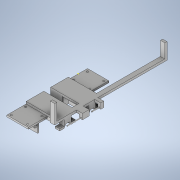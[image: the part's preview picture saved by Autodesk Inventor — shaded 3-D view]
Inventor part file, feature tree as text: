
AUTODESK INVENTOR PART (.ipt)
format: ipt  version: 2020.2 (Build 242310000, 310)  size: 751,104 bytes
history: native  units: mm
features: sketch x33, extrude x33, projected_geometry x12, hole x3
ambient origin geometry x8: Origin, YZ Plane, XZ Plane, XY Plane, X Axis, Y Axis, Z Axis, Center Point
bodies: Solid1 (feature_tree)
feature tree (81):
  sketch  "Sketch1"  dims[d0=8.0mm d1=98.298mm]
  extrude  "Extrusion1"  Depth=98.298mm
  extrude  "Extrusion2"  Depth=4.0mm
  extrude  "Extrusion3"  Depth=4.0mm TaperAngle=0.0deg
  extrude  "Extrusion4"  Depth=34.0mm
  extrude  "Extrusion5"  Depth=12.7mm
  extrude  "Extrusion6"  Depth=25.0mm
  hole  "Hole1"  [1 undecoded]
  extrude  "Extrusion11"  TaperAngle=60.0deg  [1 undecoded]
  extrude  "Extrusion12"  TaperAngle=120.0deg  [1 undecoded]
  sketch  "Sketch16"  dims[d19=6.4262mm d20=120.0deg]
  extrude  "Extrusion13"  Depth=6.4262mm
  extrude  "Extrusion14"  Depth=6.4262mm
  sketch  "Sketch17"  dims[d21=120.0deg d22=6.4262mm]
  extrude  "Extrusion15"  Depth=25.4mm TaperAngle=0.0deg
  extrude  "Extrusion18"  Depth=6.0mm
  extrude  "Extrusion19"  Depth=8.89mm
  extrude  "Extrusion20"  Depth=10.0mm
  hole  "Hole2"  [1 undecoded]
  extrude  "Extrusion21"  Depth=2.0mm
  extrude  "Extrusion22"  Depth=2.0mm
  sketch  "Sketch27"  dims[d45=8.89mm d46=2.0mm]
  extrude  "Extrusion23"  Depth=25.4mm
  extrude  "Extrusion24"  Depth=32.48mm
  extrude  "Extrusion25"  TaperAngle=90.0deg  [1 undecoded]
  sketch  "Sketch29"  dims[d79=51.53mm d80=32.48mm]
  extrude  "Extrusion26"  Depth=2.0mm
  extrude  "Extrusion27"  Depth=21.0mm
  extrude  "Extrusion28"  Depth=36.0mm TaperAngle=0.0deg
  extrude  "Extrusion29"  Depth=8.0mm
  extrude  "Extrusion30"  Depth=17.5mm
  extrude  "Extrusion32"  Depth=35.0mm
  extrude  "Extrusion33"  Depth=5.0mm
  extrude  "Extrusion34"  TaperAngle=90.0deg  [1 undecoded]
  extrude  "Extrusion35"  Depth=5.0mm
  extrude  "Extrusion38"  Depth=25.4mm TaperAngle=0.0deg
  extrude  "Extrusion39"  Depth=1.5mm
  extrude  "Extrusion40"  TaperAngle=0.0deg  [1 undecoded]
  hole  "Hole4"  [1 undecoded]
  extrude  "Extrusion43"  Depth=28.8036mm
  extrude  "Extrusion44"  Depth=25.4mm TaperAngle=0.0deg
  sketch  "Sketch2"  dims[d2=8.0mm d3=4.0mm]
  sketch  "Sketch3"  dims[d4=4.0mm d5=4.0mm d6=0.0mm]
  sketch  "Sketch4"  dims[d7=34.0mm d8=0.0mm d9=19.558mm]
  sketch  "Sketch5"  dims[d10=16.1125mm d11=12.7mm]
  sketch  "Sketch6"  dims[d12=25.0mm d13=0.0mm d14=11.1125mm]
  sketch  "Sketch14"  dims[d15=6.4135mm d16=12.827mm]
  projected_geometry  "Projected Loop2"
  sketch  "Sketch15"  dims[d17=6.4262mm d18=60.0deg]
  projected_geometry  "Projected Loop3"
  sketch  "Sketch18"  dims[d23=120.0deg d24=6.4262mm]
  sketch  "Sketch21"  dims[d25=120.0deg d26=25.4mm d27=0.0mm]
  sketch  "Sketch22"  dims[d28=6.0mm d29=8.89mm]
  sketch  "Sketch23"  dims[d30=5.9944mm d31=8.89mm]
  sketch  "Sketch24"  dims[d32=25.4mm d33=0.0mm d34=10.0mm]
  sketch  "Sketch25"  dims[d35=90.0deg d36=20.0mm]
  projected_geometry  "Projected Loop5"
  sketch  "Sketch26"  dims[d37=3.4mm d38=19.05mm d39=6.2992mm d40=6.35mm d41=90.0deg d42=5.0mm d43=0.0mm d44=2.0mm]
  sketch  "Sketch28"  dims[d47=25.4mm d48=0.0mm d78=16.24mm]
  sketch  "Sketch30"  dims[d81=90.0deg d82=90.0deg]
  sketch  "Sketch32"  dims[d83=4.0mm d84=0.0mm d87=2.0mm]
  projected_geometry  "Projected Loop6"
  sketch  "Sketch33"  dims[d88=2.0mm d89=21.0mm]
  projected_geometry  "Projected Loop7"
  sketch  "Sketch35"  dims[d90=2.0mm d91=36.0mm d92=0.0mm]
  projected_geometry  "Projected Loop8"
  sketch  "Sketch36"  dims[d93=13.878mm d94=8.0mm]
  sketch  "Sketch37"  dims[d95=180.0deg d96=17.5mm]
  sketch  "Sketch38"  dims[d97=90.0deg d98=35.0mm]
  sketch  "Sketch42"  dims[d99=3.5mm d100=5.0mm]
  sketch  "Sketch43"  dims[d101=7.0mm d102=90.0deg]
  projected_geometry  "Projected Loop9"
  projected_geometry  "Projected Loop10"
  projected_geometry  "Projected Loop11"
  projected_geometry  "Projected Loop12"
  sketch  "Sketch44"  dims[d103=5.0mm d104=3.4mm]
  sketch  "Sketch45"  dims[d105=3.4mm d106=25.4mm d107=0.0mm]
  sketch  "Sketch48"  dims[d108=6.4262mm d109=0.0mm d110=1.5mm]
  sketch  "Sketch49"  dims[d111=1.5mm d112=0.0mm d113=0.0mm d128=44.8mm d129=28.8036mm d130=25.4mm d131=0.0mm d132=3.2131mm d133=6.4262mm d134=120.0deg d135=3.2131mm d136=6.4262mm d137=120.0deg d138=25.4mm d139=0.0mm d140=8.001mm d141=13.8938mm d142=8.001mm d143=0.0mm d144=25.4mm d145=0.0mm d146=10.0mm d147=20.0mm d148=3.4mm d149=19.05mm d150=6.2992mm d151=6.35mm d152=90.0deg d153=5.0mm d154=0.0mm d155=16.2433mm d156=32.4866mm d157=51.5366mm d158=4.0mm d159=0.0mm d160=21.0mm d161=2.0mm d162=2.0mm d163=2.0mm d164=2.0mm d165=36.0mm d166=0.0mm d167=7.0mm d168=5.0mm d169=5.0mm d170=17.5mm d171=35.0mm d172=3.4mm d173=3.4mm d174=5.0mm d175=0.0mm d176=5.0mm d177=0.0mm d178=1.5mm d179=1.5mm d180=25.4mm d181=0.0mm d182=19.05mm d183=10.0mm d184=5.08mm d185=4.0mm d186=0.0mm d187=10.0mm d188=0.0mm d189=2.0mm d190=2.0mm d191=25.4mm d192=0.0mm d194=30.0mm d195=0.0mm d196=99.06mm d197=0.0mm d201=11.43mm d202=0.0mm d203=25.4mm d204=0.0mm d205=25.4mm d206=0.0mm d207=25.4mm d208=0.0mm d239=25.4mm d240=0.0mm d241=1.5mm d242=0.0mm d243=39.0mm d244=35.0mm d245=39.0mm d246=35.0mm d247=3.0mm d248=0.0mm d249=5.0mm d250=5.0mm d251=29.7mm d252=26.05mm d253=4.0mm d254=4.0mm d255=29.7mm d256=26.05mm d257=3.4mm d258=19.05mm d259=6.2992mm d260=6.35mm d261=90.0deg d262=25.4mm d263=20.594885mm d271=4.0mm d272=25.4mm d273=0.0mm d274=25.4mm d275=0.0mm d214=12.7mm d215=0.872665mm d216=12.7mm d217=0.872665mm d228=12.7mm d229=0.872665mm d230=12.7mm d231=0.872665mm]
  projected_geometry  "Projected Loop13"
  projected_geometry  "Projected Loop14"
note: 8 required parameter values undecoded (feature->parameter linkage not recoverable at this tier; creation-order binding heuristic only, values carry confidence <= 0.55)
